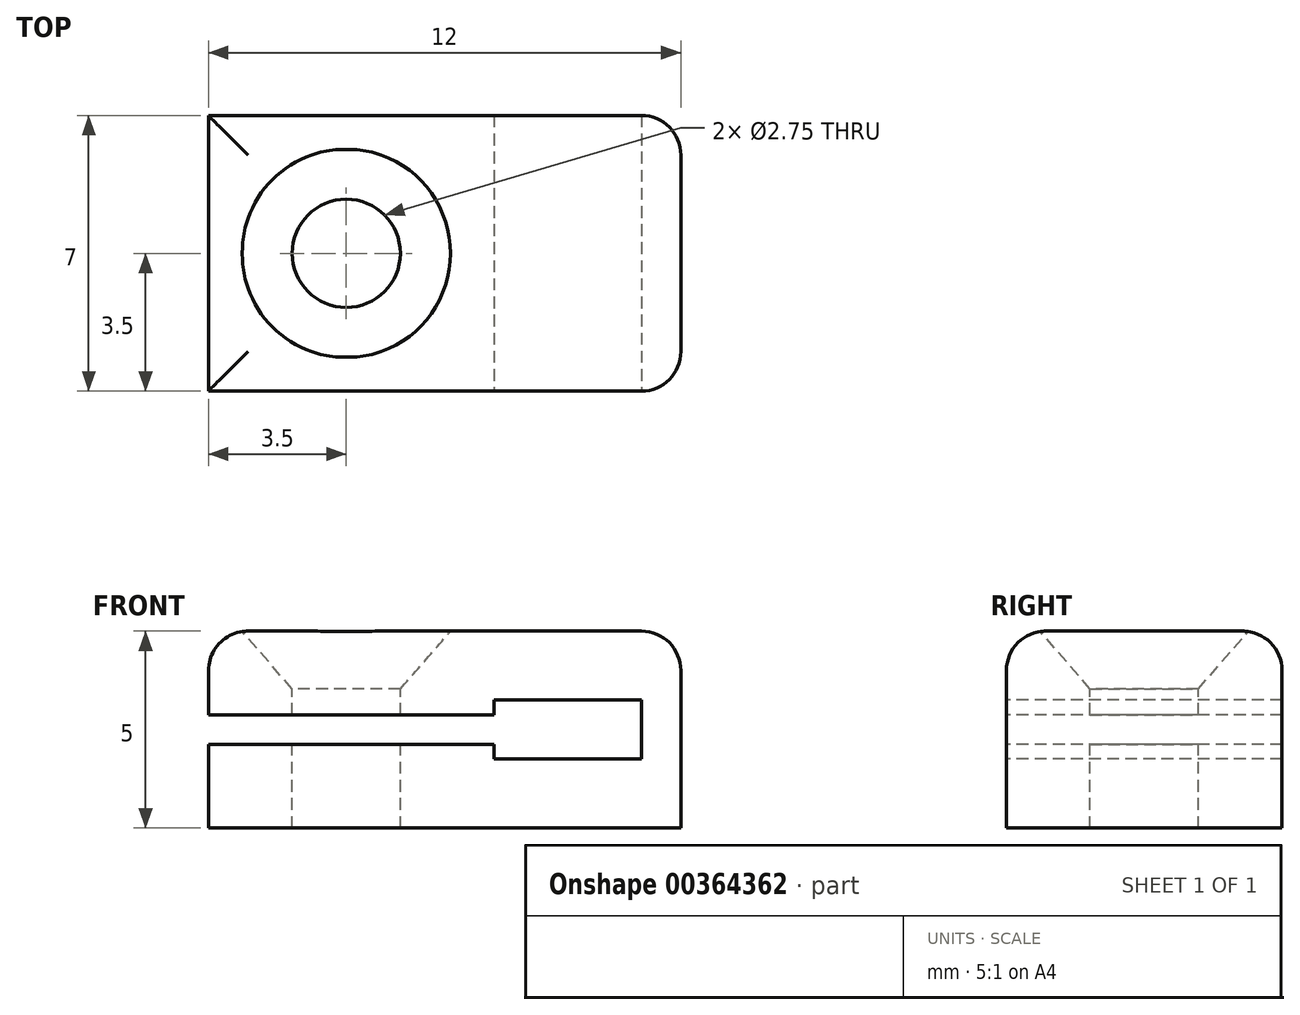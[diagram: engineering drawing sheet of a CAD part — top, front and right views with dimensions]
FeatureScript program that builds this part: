
annotation { "Feature Type Name" : "Feature", "Feature Type Description" : "" }
export const myFeature = defineFeature(function(context is Context, id is Id, definition is map)
    precondition{}
    {
        {
            var Q0;
            Q0=qCreatedBy(makeId("Top.planeOp"),FACE);
            var sketch = newSketch(context, id + "F0", { "sketchPlane" : qUnion([Q0])});
            skLineSegment(sketch, "E0.bottom", {"start": v(6, -3.5) * mm, "end": v(-6, -3.5) * mm});
            skLineSegment(sketch, "E0.top", {"start": v(6, 3.5) * mm, "end": v(-6, 3.5) * mm});
            skLineSegment(sketch, "E0.left", {"start": v(6, -3.5) * mm, "end": v(6, 3.5) * mm});
            skLineSegment(sketch, "E0.right", {"start": v(-6, -3.5) * mm, "end": v(-6, 3.5) * mm});
            skPoint(sketch, "E0.middle", {"position": v(0, 0) * mm});
            skLineSegment(sketch, "E1", {"start": v(1, 3.5) * mm, "end": v(1, -3.5) * mm});
            skPoint(sketch, "E2", {"position": v(-2.5, 0) * mm});
            skSolve(sketch);
        }
        {
            var Q0;
            {var subQ0=sQuery(id+"F0.wireOp",EDGE,"E0.left");Q0=makeQuery(id+"F0.imprint","IMPRINT",FACE,{"disambiguationData":[TD([[makeQuery(id+"F0.imprint","IMPRINT",EDGE,{"derivedFrom":subQ0}),1.0]])]});}
            var Q1;
            {var subQ0=sQuery(id+"F0.wireOp",EDGE,"E0.right");Q1=makeQuery(id+"F0.imprint","IMPRINT",FACE,{"disambiguationData":[TD([[makeQuery(id+"F0.imprint","IMPRINT",EDGE,{"derivedFrom":subQ0}),-1.0]])]});}
            extrude(context, id + "F1", {"entities" : qUnion([Q0, Q1]), "oppositeDirection" : true, "depth" : 5 * mm});
        }
        {
            var Q0;
            Q0=makeQuery(id+"F1.opExtrude","CAP_FACE",FACE,{"disambiguationData":[OSD([sQuery(id+"F0.wireOp",EDGE,"E0.bottom"),sQuery(id+"F0.wireOp",EDGE,"E0.top"),sQuery(id+"F0.wireOp",EDGE,"E0.left"),sQuery(id+"F0.wireOp",EDGE,"E0.right")])],"isStart":true});
            var sketch = newSketch(context, id + "F2", { "sketchPlane" : qUnion([Q0])});
            skPoint(sketch, "E3", {"position": v(-2.5, 0) * mm});
            skPoint(sketch, "E3.positionSnap0", {"position": v(-6, 0) * mm});
            skSolve(sketch);
        }
        {
            var Q0;
            Q0=sQuery(id+"F2.wireOp",VERTEX,"E3");
            var Q1;
            Q1=makeQuery(id+"F1.opExtrude","SWEPT_BODY",BODY,{"disambiguationData":[OSD([sQuery(id+"F0.wireOp",EDGE,"E0.bottom"),sQuery(id+"F0.wireOp",EDGE,"E0.top"),sQuery(id+"F0.wireOp",EDGE,"E0.left"),sQuery(id+"F0.wireOp",EDGE,"E0.right")])]});
            hole(context, id + "F3", {"style" : HoleStyle.C_SINK, "endStyle" : HoleEndStyle.THROUGH, "holeDiameter" : 2.75 * mm, "cSinkDiameter" : 5.3 * mm, "cSinkAngle" : 82 * degree, "isTappedThrough" : true, "tappedDepth" : 12 * mm, "tapClearance" : 3, "locations" : qUnion([Q0]), "scope" : qUnion([Q1])});
        }
        {
            var Q0;
            Q0=makeQuery(id+"F1.opExtrude","SWEPT_FACE",FACE,{"disambiguationData":[OSD([sQuery(id+"F0.wireOp",EDGE,"E0.bottom")])]});
            var sketch = newSketch(context, id + "F4", { "sketchPlane" : qUnion([Q0])});
            skLineSegment(sketch, "E4.left", {"start": v(5, -3.25) * mm, "end": v(5, -1.75) * mm});
            skPoint(sketch, "E4.middle", {"position": v(-6, -2.5) * mm});
            skLineSegment(sketch, "E5", {"start": v(1.25, -2.13) * mm, "end": v(-6, -2.13) * mm});
            skLineSegment(sketch, "E6", {"start": v(1.25, -2.88) * mm, "end": v(-6, -2.88) * mm});
            skLineSegment(sketch, "E7", {"start": v(1.25, 0) * mm, "end": v(1.25, -5) * mm, "construction": true});
            skPoint(sketch, "E8", {"position": v(1.25, -2.13) * mm});
            skPoint(sketch, "E9", {"position": v(1.25, -2.88) * mm});
            skLineSegment(sketch, "E10", {"start": v(-6, -2.5) * mm, "end": v(6, -2.5) * mm, "construction": true});
            skLineSegment(sketch, "E11", {"start": v(1.25, -2.13) * mm, "end": v(1.25, -1.75) * mm});
            skLineSegment(sketch, "E12", {"start": v(1.25, -1.75) * mm, "end": v(5, -1.75) * mm});
            skLineSegment(sketch, "E13", {"start": v(1.25, -2.88) * mm, "end": v(1.25, -3.25) * mm});
            skLineSegment(sketch, "E14", {"start": v(1.25, -3.25) * mm, "end": v(5, -3.25) * mm});
            skSolve(sketch);
        }
        {
            var Q0;
            Q0=makeQuery(id+"F4.imprint","IMPRINT",FACE,{"disambiguationData":[TD([[makeQuery(id+"F4.imprint","IMPRINT",EDGE,{"derivedFrom":sQuery(id+"F4.wireOp",EDGE,"E4.left")}),1.0]])]});
            var Q1;
            Q1=makeQuery(id+"F1.opExtrude","SWEPT_FACE",FACE,{"disambiguationData":[OSD([sQuery(id+"F0.wireOp",EDGE,"E0.top")])]});
            extrude(context, id + "F5", {"entities" : qUnion([Q0]), "operationType" : NewBodyOperationType.REMOVE, "endBound" : BoundingType.UP_TO_SURFACE, "oppositeDirection" : true, "endBoundEntityFace" : qUnion([Q1]), "depth" : 25 * mm});
        }
        {
            var Q0;
            Q0=makeQuery(id+"F1.opExtrude","CAP_EDGE",EDGE,{"disambiguationData":[OSD([sQuery(id+"F0.wireOp",EDGE,"E0.right")])],"isStart":true});
            var Q1;
            Q1=makeQuery(id+"F1.opExtrude","CAP_EDGE",EDGE,{"disambiguationData":[OSD([sQuery(id+"F0.wireOp",EDGE,"E0.top")])],"isStart":true});
            var Q2;
            Q2=makeQuery(id+"F1.opExtrude","CAP_EDGE",EDGE,{"disambiguationData":[OSD([sQuery(id+"F0.wireOp",EDGE,"E0.left")])],"isStart":true});
            var Q3;
            Q3=makeQuery(id+"F1.opExtrude","CAP_EDGE",EDGE,{"disambiguationData":[OSD([sQuery(id+"F0.wireOp",EDGE,"E0.bottom")])],"isStart":true});
            var Q4;
            Q4=makeQuery(id+"F1.opExtrude","SWEPT_EDGE",EDGE,{"disambiguationData":[OSD([sQuery(id+"F0.wireOp",EDGE,"E0.bottom"),sQuery(id+"F0.wireOp",EDGE,"E0.left")])]});
            var Q5;
            Q5=makeQuery(id+"F1.opExtrude","SWEPT_EDGE",EDGE,{"disambiguationData":[OSD([sQuery(id+"F0.wireOp",EDGE,"E0.top"),sQuery(id+"F0.wireOp",EDGE,"E0.left")])]});
            fillet(context, id + "F6", {"entities" : qUnion([Q0, Q1, Q2, Q3, Q4, Q5]), "radius" : 1 * mm, "tangentPropagation" : true, "allowEdgeOverflow" : false});
        }
    });
